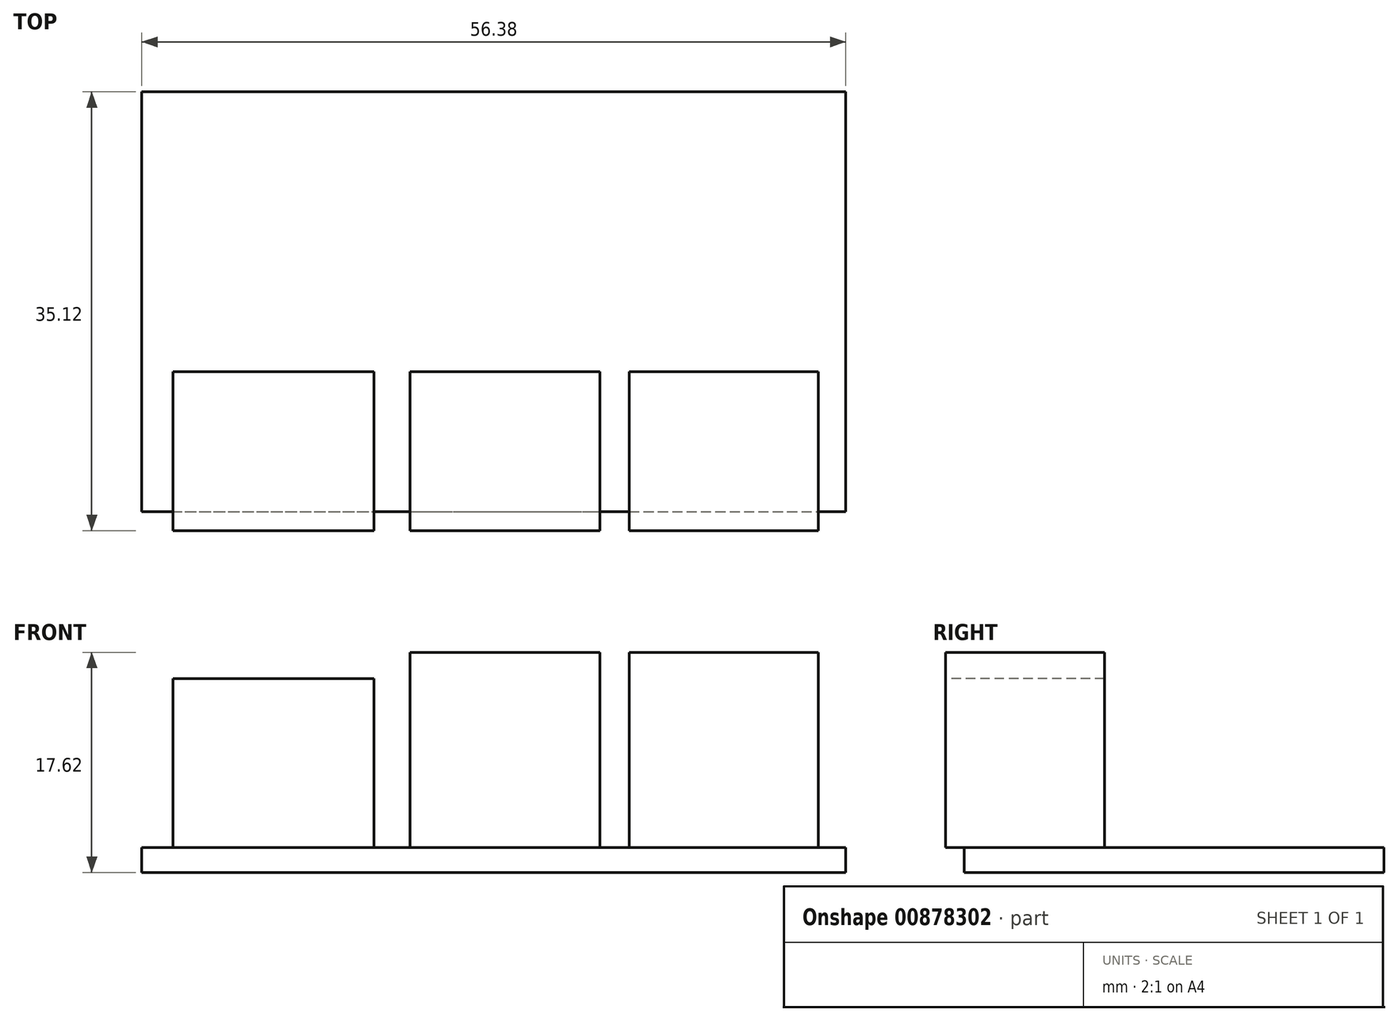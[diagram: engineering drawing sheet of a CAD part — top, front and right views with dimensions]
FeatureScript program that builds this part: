
annotation { "Feature Type Name" : "Feature", "Feature Type Description" : "" }
export const myFeature = defineFeature(function(context is Context, id is Id, definition is map)
    precondition{}
    {
        {
            var Q0;
            Q0=qCreatedBy(makeId("Top.planeOp"),FACE);
            var sketch = newSketch(context, id + "F0", { "sketchPlane" : qUnion([Q0])});
            skLineSegment(sketch, "E0.bottom", {"start": v(-34.2, 18.97) * mm, "end": v(22.2, 18.97) * mm});
            skLineSegment(sketch, "E0.top", {"start": v(-34.2, -14.65) * mm, "end": v(22.2, -14.65) * mm});
            skLineSegment(sketch, "E0.left", {"start": v(-34.2, 18.97) * mm, "end": v(-34.2, -14.65) * mm});
            skLineSegment(sketch, "E0.right", {"start": v(22.2, 18.97) * mm, "end": v(22.2, -14.65) * mm});
            skSolve(sketch);
        }
        {
            var Q0;
            Q0=makeQuery(id+"F0.imprint","IMPRINT",FACE,{"disambiguationData":[TD([[makeQuery(id+"F0.imprint","IMPRINT",EDGE,{"derivedFrom":sQuery(id+"F0.wireOp",EDGE,"E0.bottom")}),-1.0]])]});
            extrude(context, id + "F1", {"entities" : qUnion([Q0]), "depth" : 2 * mm, "offsetDistance" : 25 * mm});
        }
        {
            var Q0;
            Q0=makeQuery(id+"F1.opExtrude","CAP_FACE",FACE,{"disambiguationData":[OSD([sQuery(id+"F0.wireOp",EDGE,"E0.bottom"),sQuery(id+"F0.wireOp",EDGE,"E0.top"),sQuery(id+"F0.wireOp",EDGE,"E0.left"),sQuery(id+"F0.wireOp",EDGE,"E0.right")])],"isStart":false});
            var sketch = newSketch(context, id + "F2", { "sketchPlane" : qUnion([Q0])});
            skLineSegment(sketch, "E1.bottom", {"start": v(-31.7, -14.65) * mm, "end": v(20, -14.65) * mm});
            skLineSegment(sketch, "E1.top", {"start": v(-31.7, -3.42) * mm, "end": v(20, -3.42) * mm});
            skLineSegment(sketch, "E1.left", {"start": v(-31.7, -14.65) * mm, "end": v(-31.7, -3.42) * mm});
            skLineSegment(sketch, "E1.right", {"start": v(20, -14.65) * mm, "end": v(20, -3.42) * mm});
            skSolve(sketch);
        }
        {
            var Q0;
            Q0=makeQuery(id+"F2.imprint","IMPRINT",FACE,{"disambiguationData":[TD([[makeQuery(id+"F2.imprint","IMPRINT",EDGE,{"derivedFrom":sQuery(id+"F2.wireOp",EDGE,"E1.bottom")}),1.0]])]});
            extrude(context, id + "F3", {"entities" : qUnion([Q0]), "operationType" : NewBodyOperationType.ADD, "depth" : 15.62 * mm, "offsetDistance" : 25 * mm});
        }
        {
            var Q0;
            Q0=makeQuery(id+"F3.boolean.opBoolean","MERGE",FACE,{"derivedFrom":[makeQuery(id+"F1.opExtrude","SWEPT_FACE",FACE,{"disambiguationData":[OSD([sQuery(id+"F0.wireOp",EDGE,"E0.top")])]}),makeQuery(id+"F3.opExtrude","SWEPT_FACE",FACE,{"disambiguationData":[OSD([sQuery(id+"F2.wireOp",EDGE,"E1.bottom")])]})]});
            var sketch = newSketch(context, id + "F4", { "sketchPlane" : qUnion([Q0])});
            skLineSegment(sketch, "E2.bottom", {"start": v(-31.7, 17.62) * mm, "end": v(20, 17.62) * mm});
            skLineSegment(sketch, "E2.top", {"start": v(-31.7, 2) * mm, "end": v(20, 2) * mm});
            skLineSegment(sketch, "E2.left", {"start": v(-31.7, 17.62) * mm, "end": v(-31.7, 2) * mm});
            skLineSegment(sketch, "E2.right", {"start": v(20, 17.62) * mm, "end": v(20, 2) * mm});
            skSolve(sketch);
        }
        {
            var Q0;
            Q0 = qSketchRegion(id + "F4", true);
            extrude(context, id + "F5", {"entities" : qUnion([Q0]), "operationType" : NewBodyOperationType.ADD, "depth" : 1.5 * mm, "offsetDistance" : 25 * mm});
        }
        {
            var Q0;
            Q0=makeQuery(id+"F5.opExtrude","CAP_FACE",FACE,{"disambiguationData":[OSD([sQuery(id+"F4.wireOp",EDGE,"E2.bottom"),sQuery(id+"F4.wireOp",EDGE,"E2.top"),sQuery(id+"F4.wireOp",EDGE,"E2.left"),sQuery(id+"F4.wireOp",EDGE,"E2.right")])],"isStart":false});
            var sketch = newSketch(context, id + "F6", { "sketchPlane" : qUnion([Q0])});
            skLineSegment(sketch, "E3.bottom", {"start": v(-31.7, 15.52) * mm, "end": v(-12.7, 15.52) * mm});
            skLineSegment(sketch, "E3.top", {"start": v(-31.7, 17.62) * mm, "end": v(-12.7, 17.62) * mm});
            skLineSegment(sketch, "E3.left", {"start": v(-31.7, 15.52) * mm, "end": v(-31.7, 17.62) * mm});
            skLineSegment(sketch, "E3.right", {"start": v(-12.7, 15.52) * mm, "end": v(-12.7, 17.62) * mm});
            skLineSegment(sketch, "E4.bottom", {"start": v(-15.6, 2) * mm, "end": v(-12.7, 2) * mm});
            skLineSegment(sketch, "E4.top", {"start": v(-15.6, 17.62) * mm, "end": v(-12.7, 17.62) * mm});
            skLineSegment(sketch, "E4.left", {"start": v(-15.6, 2) * mm, "end": v(-15.6, 17.62) * mm});
            skLineSegment(sketch, "E4.right", {"start": v(-12.7, 2) * mm, "end": v(-12.7, 17.62) * mm});
            skLineSegment(sketch, "E5.bottom", {"start": v(2.5, 17.62) * mm, "end": v(4.85, 17.62) * mm});
            skLineSegment(sketch, "E5.top", {"start": v(2.5, 2) * mm, "end": v(4.85, 2) * mm});
            skLineSegment(sketch, "E5.left", {"start": v(2.5, 17.62) * mm, "end": v(2.5, 2) * mm});
            skLineSegment(sketch, "E5.right", {"start": v(4.85, 17.62) * mm, "end": v(4.85, 2) * mm});
            skSolve(sketch);
        }
        {
            var Q0;
            {var subQ4=sQuery(id+"F6.wireOp",EDGE,"E3.top");Q0=makeQuery(id+"F6.imprint","IMPRINT",FACE,{"disambiguationData":[TD([[makeQuery(id+"F6.imprint","IMPRINT",EDGE,{"derivedFrom":subQ4}),-1.0]])]});}
            var Q1;
            {var subQ5=sQuery(id+"F6.wireOp",EDGE,"E4.top");Q1=makeQuery(id+"F6.imprint","IMPRINT",FACE,{"disambiguationData":[TD([[makeQuery(id+"F6.imprint","IMPRINT",EDGE,{"derivedFrom":subQ5}),-1.0]])]});}
            var Q2;
            {var subQ5=sQuery(id+"F6.wireOp",EDGE,"E4.bottom");Q2=makeQuery(id+"F6.imprint","IMPRINT",FACE,{"disambiguationData":[TD([[makeQuery(id+"F6.imprint","IMPRINT",EDGE,{"derivedFrom":subQ5}),1.0]])]});}
            var Q3;
            Q3=makeQuery(id+"F6.imprint","IMPRINT",FACE,{"disambiguationData":[TD([[makeQuery(id+"F6.imprint","IMPRINT",EDGE,{"derivedFrom":sQuery(id+"F6.wireOp",EDGE,"E5.bottom")}),-1.0]])]});
            extrude(context, id + "F7", {"entities" : qUnion([Q0, Q1, Q2, Q3]), "operationType" : NewBodyOperationType.REMOVE, "oppositeDirection" : true, "depth" : 17 * mm, "offsetDistance" : 25 * mm});
        }
    });
